# Revit family: Gleiter radial-axial GL-100 o.Lasche, 2xAG
name_source: partatom
category: HLS-Bauteile
revit_build: Autodesk Revit 2017 (Build: 20190507_1515(x64)
units: mm (PartAtom-declared; Revit-internal decimal feet)

## family parameters
Arbeitsebenenbasiert = Ja
Beim Laden mit Abzugskörper schneiden = Nein
Bemaßung runder Anschluss = Durchmesser verwenden
Gemeinsam genutzt = Ja
Immer vertikal = Nein
Raumberechnungspunkt = Nein
Teiletyp = Normal

## types (4) — shared parameters
B1 = 36 mm  [stored 0.11811 ft]
Breite = 90 mm  [stored 0.295276 ft]
C = 18 mm
D0 = 14 mm  [stored 0.0459318 ft]
Fabrikat = MEFA
Gleitreibungsfaktor = 0.15 - 0.25
H1 = 11 mm  [stored 0.0360892 ft]
Haftreibungsfaktor = 0,2 - 0,3
Kurztext1 = Gleitelement radial-axial GL 100
L = 72 mm  [stored 0.23622 ft]
Länge = 160 mm  [stored 0.524934 ft]
Material Gleitstreifen = Kunststoff
Materialname Gleitstreifen = Polyamid 6
Mengeneinheit = St
Vorgabe-Ansicht = 1219 mm
max. Temperaturbeständigkeit = 100 °C
vpe = 1 St

## per-type parameters (varying)
| type | Artikelnummer | EAN | GL-100 o.Lasche, 2xAG | Gewicht | Gewicht pro Bauteil | H | Kurztext2 |
| Gleiter ra-ax GL100 o. Lasche, 2x M10 | 077048001 | 4250928417688 | Gleiter GL-100 o. Lasche, 2xAG : Gleiter GL-100, 2x AG M10 | 0.69 kg | 0.69 kg | 42 mm  [stored 0.137795 ft] | Anschluss 2 x M10 ohne Lasche |
| Gleiter ra-ax GL100 o. Lasche, 2x M12 | 077048101 | 4250928417701 | Gleiter GL-100 o. Lasche, 2xAG : Gleiter GL-100, 2x AG M12 | 0.72 kg | 0.72 kg | 44 mm  [stored 0.144357 ft] | Anschluss 2 x M12 ohne Lasche |
| Gleiter ra-ax GL100 o. Lasche, 2x M16 | 077048701 | 4250928417824 | Gleiter GL-100 o. Lasche, 2xAG : Gleiter GL-100, 2x AG M16 | 0.73 kg | 0.73 kg | 43 mm  [stored 0.141076 ft] | Anschluss 2 x M16 ohne Lasche |
| Gleiter ra-ax GL100 o. Lasche, 2x 1/2" | 077048201 | 4250928417725 | Gleiter GL-100 o. Lasche, 2xAG : Gleiter GL-100, 2x AG Muffe halbe Zoll | 0.71 kg | 0.71 kg | 43 mm  [stored 0.141076 ft] | Anschluss 2 x 1/2'' ohne Lasche |

note: [stored X ft] marks values corroborated as IEEE doubles in the binary element streams (Revit-internal decimal feet)

## geometry (parser evidence)
native form markers: Sweep x3
no freeform markers — native parametric forms only
